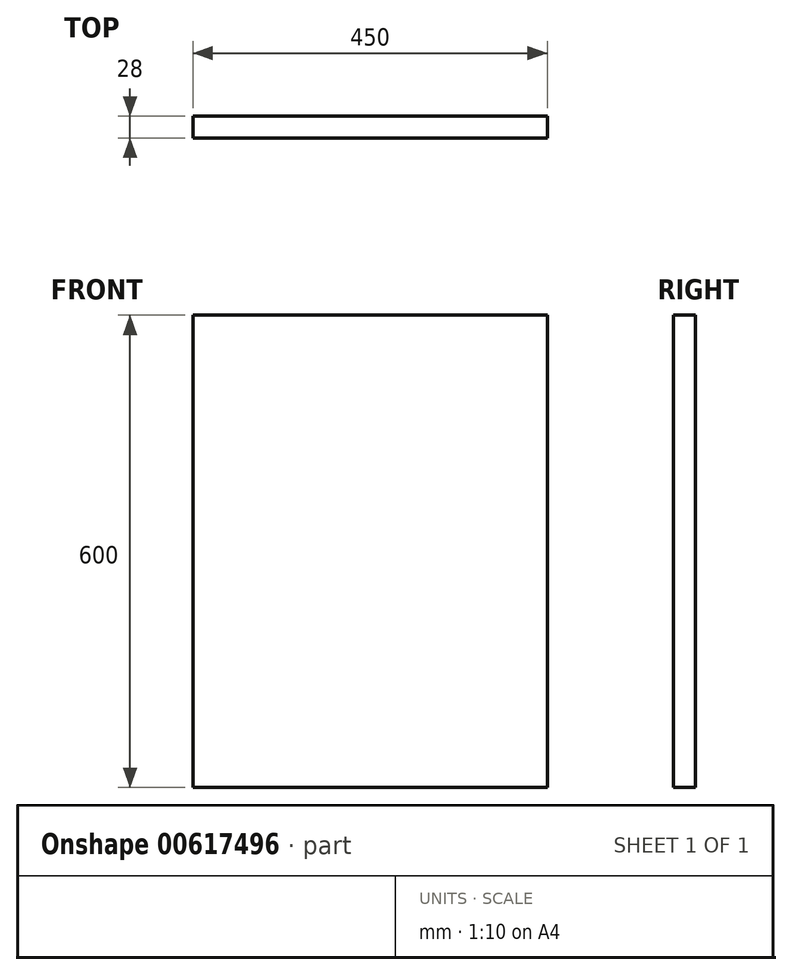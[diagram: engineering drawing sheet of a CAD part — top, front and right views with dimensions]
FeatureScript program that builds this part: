
annotation { "Feature Type Name" : "Feature", "Feature Type Description" : "" }
export const myFeature = defineFeature(function(context is Context, id is Id, definition is map)
    precondition{}
    {
        {
            var Q0;
            Q0=qCreatedBy(makeId("Top.planeOp"),FACE);
            var sketch = newSketch(context, id + "F0", { "sketchPlane" : qUnion([Q0])});
            skLineSegment(sketch, "E0.bottom", {"start": v(-225.89, -55.1) * mm, "end": v(224.11, -55.1) * mm});
            skLineSegment(sketch, "E0.top", {"start": v(-225.89, -83.1) * mm, "end": v(224.11, -83.1) * mm});
            skLineSegment(sketch, "E0.left", {"start": v(-225.89, -55.1) * mm, "end": v(-225.89, -83.1) * mm});
            skLineSegment(sketch, "E0.right", {"start": v(224.11, -55.1) * mm, "end": v(224.11, -83.1) * mm});
            skSolve(sketch);
        }
        {
            var Q0;
            Q0 = qSketchRegion(id + "F0", true);
            extrude(context, id + "F1", {"entities" : qUnion([Q0]), "oppositeDirection" : true, "depth" : 600 * mm, "offsetDistance" : 25 * mm});
        }
    });
